# Revit family: Downlight - Spot
name_source: partatom
category: Lighting Fixtures
revit_build: Autodesk Revit Architecture 2012 (Build: 20110210_1515)
units: mm (PartAtom-declared; Revit-internal decimal feet)

## types (6) — shared parameters
Apparent Load = 40 VA
Assembly Code = D5020230
Ballast Number of Poles = 1
Color Filter = 16777215
Dimming Lamp Color Temperature Shift = <None>
Lamp Half Width = 0' - 2"
Lamp Height = 0' - 3"
Lamp Width = 0' - 4"
Light Casing Material = Plastic - Black
Load Classification = Lighting - Dwelling Unit
Spot Beam Angle = 30.00°
Spot Field Angle = 90.00°
Wattage Comments = 40

## per-type parameters (varying)
| type | Ballast Voltage | Light Source Symbol Length | Tilt Angle |
| 90 Degree Tilt - 277V | 277 V | 10' - 0" | 90.00° |
| 75 Degree Tilt - 277V | 277 V | 10' - 0" | 75.00° |
| 60 Degree Tilt - 120V | 120 V | 4' - 0" | 60.00° |
| 60 Degree Tilt - 277V | 277 V | 10' - 0" | 60.00° |
| 75 Degree Tilt - 120V | 120 V | 10' - 0" | 75.00° |
| 90 Degree Tilt - 120V | 120 V | 10' - 0" | 90.00° |

## geometry (parser evidence)
native form markers: Blend x2, Sweep x1
no freeform markers — native parametric forms only
